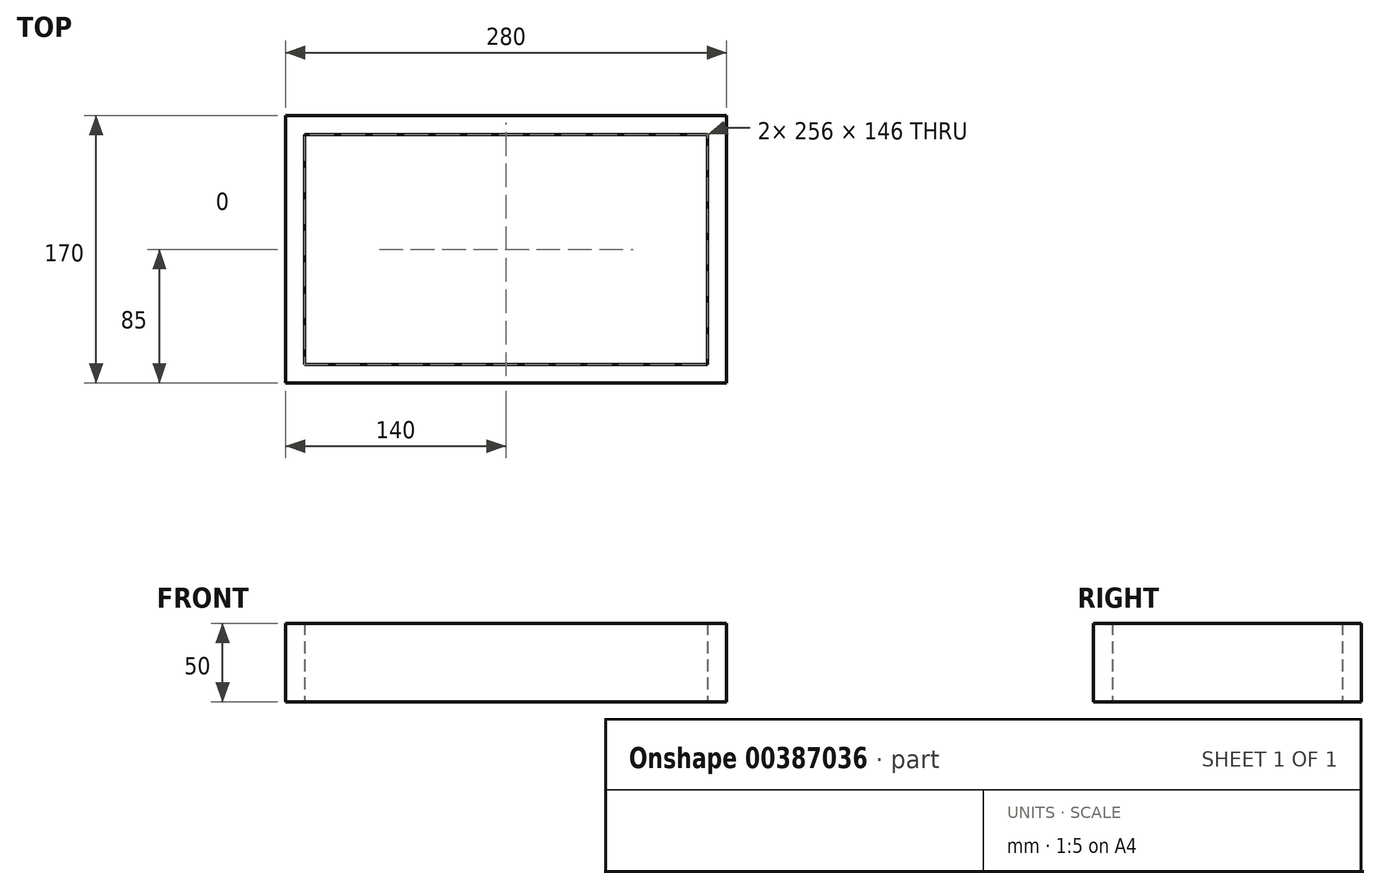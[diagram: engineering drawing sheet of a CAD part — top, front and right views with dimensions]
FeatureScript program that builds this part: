
annotation { "Feature Type Name" : "Feature", "Feature Type Description" : "" }
export const myFeature = defineFeature(function(context is Context, id is Id, definition is map)
    precondition{}
    {
        {
            var Q0;
            Q0=qCreatedBy(makeId("Top.planeOp"),FACE);
            var sketch = newSketch(context, id + "F0", { "sketchPlane" : qUnion([Q0])});
            skLineSegment(sketch, "E0.bottom", {"start": v(140, 85) * mm, "end": v(-140, 85) * mm});
            skLineSegment(sketch, "E0.top", {"start": v(140, -85) * mm, "end": v(-140, -85) * mm});
            skLineSegment(sketch, "E0.left", {"start": v(140, 85) * mm, "end": v(140, -85) * mm});
            skLineSegment(sketch, "E0.right", {"start": v(-140, 85) * mm, "end": v(-140, -85) * mm});
            skPoint(sketch, "E0.middle", {"position": v(0, 0) * mm});
            skLineSegment(sketch, "E1.0", {"start": v(128, -73) * mm, "end": v(-128, -73) * mm});
            skLineSegment(sketch, "E1.1", {"start": v(128, 73) * mm, "end": v(128, -73) * mm});
            skLineSegment(sketch, "E1.2", {"start": v(128, 73) * mm, "end": v(-128, 73) * mm});
            skLineSegment(sketch, "E1.3", {"start": v(-128, 73) * mm, "end": v(-128, -73) * mm});
            skSolve(sketch);
        }
        {
            var Q0;
            Q0=makeQuery(id+"F0.imprint","IMPRINT",FACE,{"disambiguationData":[TD([[makeQuery(id+"F0.imprint","IMPRINT",EDGE,{"derivedFrom":sQuery(id+"F0.wireOp",EDGE,"E0.bottom")}),1.0]])]});
            extrude(context, id + "F1", {"entities" : qUnion([Q0]), "depth" : 50 * mm});
        }
    });
